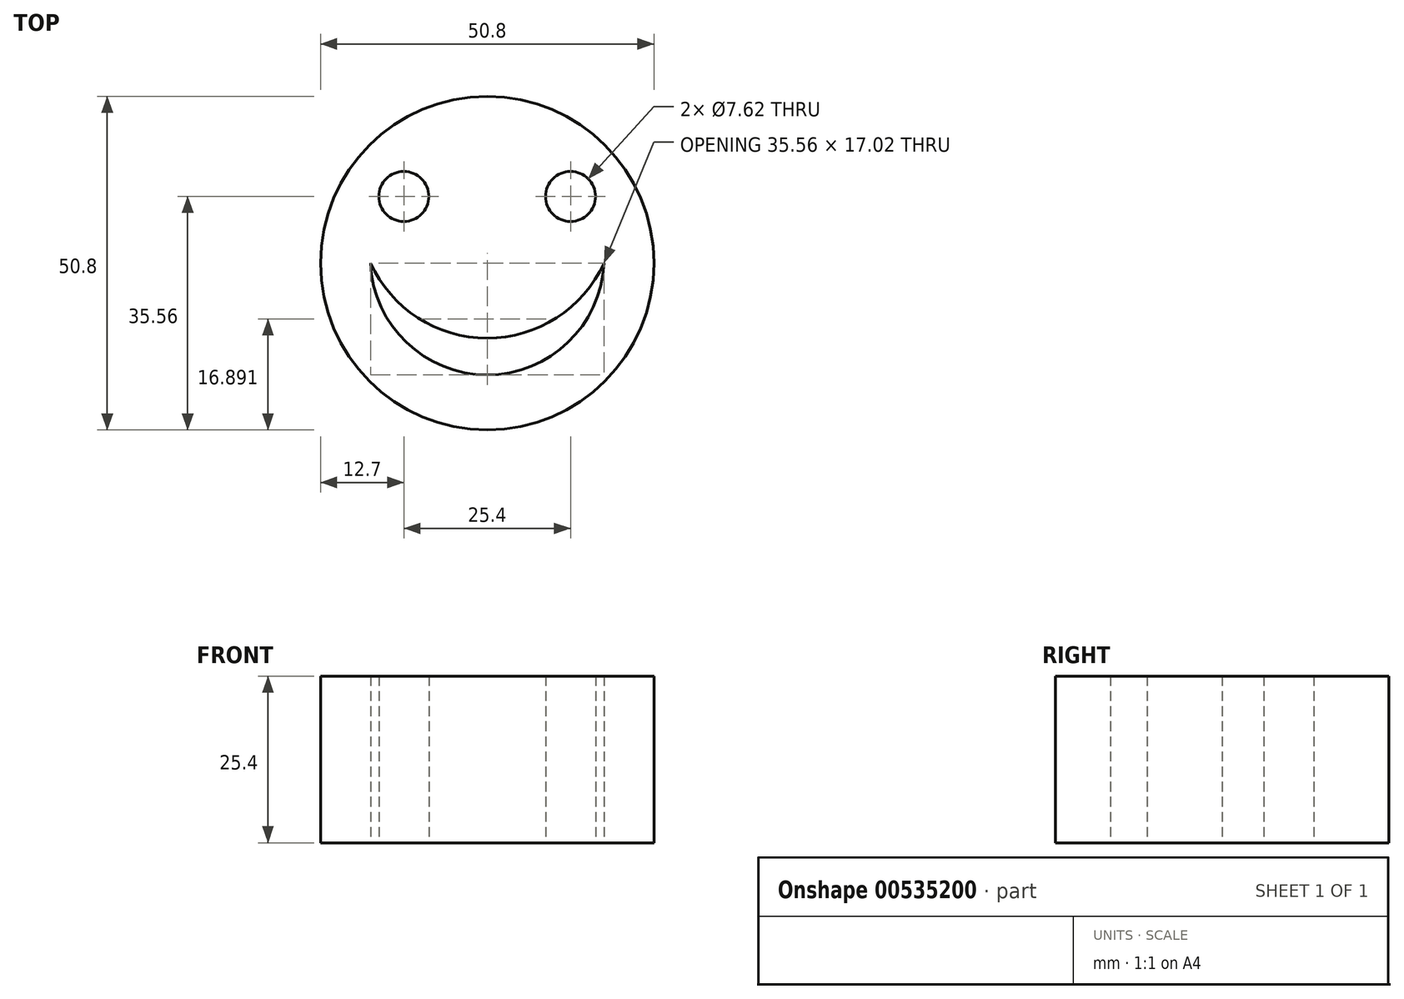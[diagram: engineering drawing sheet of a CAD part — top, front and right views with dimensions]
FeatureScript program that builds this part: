
annotation { "Feature Type Name" : "Feature", "Feature Type Description" : "" }
export const myFeature = defineFeature(function(context is Context, id is Id, definition is map)
    precondition{}
    {
        {
            var Q0;
            Q0=qCreatedBy(makeId("Top.planeOp"),FACE);
            var sketch = newSketch(context, id + "F0", { "sketchPlane" : qUnion([Q0])});
            skCircle(sketch, "E0", {"center": v(0, 0) * mm, "radius": 25.4 * mm});
            skCircle(sketch, "E1", {"center": v(-12.7, 10.16) * mm, "radius": 3.81 * mm});
            skCircle(sketch, "E2", {"center": v(12.7, 10.16) * mm, "radius": 3.81 * mm});
            skLineSegment(sketch, "E3.bottom", {"start": v(0, 0) * mm, "end": v(12.7, 0) * mm, "construction": true});
            skLineSegment(sketch, "E3.top", {"start": v(0, 10.16) * mm, "end": v(12.7, 10.16) * mm, "construction": true});
            skLineSegment(sketch, "E3.left", {"start": v(0, 0) * mm, "end": v(0, 10.16) * mm});
            skLineSegment(sketch, "E3.right", {"start": v(12.7, 0) * mm, "end": v(12.7, 10.16) * mm, "construction": true});
            skLineSegment(sketch, "E4.bottom", {"start": v(0, 0) * mm, "end": v(-12.7, 0) * mm, "construction": true});
            skLineSegment(sketch, "E4.top", {"start": v(0, 10.16) * mm, "end": v(-12.7, 10.16) * mm, "construction": true});
            skLineSegment(sketch, "E4.left", {"start": v(0, 0) * mm, "end": v(0, 10.16) * mm, "construction": true});
            skLineSegment(sketch, "E4.right", {"start": v(-12.7, 0) * mm, "end": v(-12.7, 10.16) * mm, "construction": true});
            skArc(sketch, "E5", {"start": v(-17.78, 0) * mm, "mid": v(0, -17.02) * mm, "end": v(17.78, 0) * mm});
            skPoint(sketch, "E5.startSnap0", {"position": v(-6.35, 0) * mm});
            skArc(sketch, "E6", {"start": v(-17.78, 0) * mm, "mid": v(0, -11.43) * mm, "end": v(17.78, 0) * mm});
            skSolve(sketch);
        }
        {
            var Q0;
            Q0=makeQuery(id+"F0.imprint","IMPRINT",FACE,{"disambiguationData":[TD([[makeQuery(id+"F0.imprint","IMPRINT",EDGE,{"derivedFrom":sQuery(id+"F0.wireOp",EDGE,"E0")}),1.0]])]});
            extrude(context, id + "F1", {"entities" : qUnion([Q0]), "depth" : 25.4 * mm, "offsetDistance" : 25.4 * mm});
        }
    });
